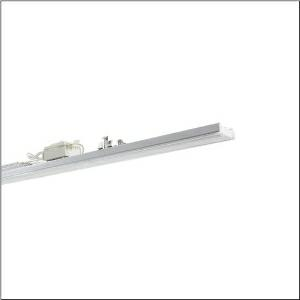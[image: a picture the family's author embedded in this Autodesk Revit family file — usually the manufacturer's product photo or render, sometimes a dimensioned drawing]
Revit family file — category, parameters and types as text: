
# Revit family: licross_r__11_recessed_mo_51tl12dn395g_1cc3
name_source: partatom
category: Lighting Fixtures
units: mm (PartAtom-declared; Revit-internal decimal feet)

## family parameters
Cut with Voids When Loaded = No
Host = Face
Light Source = No
Part Type = Normal
Room Calculation Point = No
Round Connector Dimension = Use Diameter
Shared = No

## types (1)
- --- (1 x LED, 9840 lm, 56.7 W, 3000K)
    Apparent Load = 57 VA
    CIE Flux Codes = 67 92 99 100 100
    Color Rendering = 80
    Color Temperature = 3000K
    Default Elevation = 1800 mm
    Description = Licross® 11 Recessed MO, luminaire insert, of sheet steel, coil coated, white, length: 1.500mm, width: 66mm, height: 67mm, LED rated luminous flux: 9.840lm, light colour: 830, control gear: DALI 2, with plug, 5-pole, with phase selection, mains connection: 220..240V, AC, 50/60Hz, rated input power: 57W, halogen-free wiring, primary optical cover: cover, of PMMA, light emission: direct distribution, primary light characteristic: symmetric, protection rating (complete): IP40, insulation class (complete): insulation class I (protective earthing), certification: CE, ENEC, VDE, UKCA, protection symbol: D if used in an environment without relevant dust loads with corresponding accessories, impact resistance: IK06, permissible ambient temperature for indoor applications: -25..+35°C, corresponds to IFS (International Featured Standards) requirements for safety and quality in the food industry, reducing of maximum allowable ambient temperature of 5°C with ceiling mounting, LABS conformity tested according to VDMA 24364:2018-05, packaging unit: 1 piece
    Height = 58 mm
    Lamp = 1 x LED
    Lamp Light Flux = 9840 lm
    Lamp Power = 56.7 W
    Lamp count = 1
    Length = 1500 mm
    Luminous efficacy = 174 lm/W
    Manufacturer = Siteco
    ModVariant = No
    Model = 51TL12DN395G
    Mounting Place = Ceiling
    Mounting Type = Pendant
    Number of Poles = 1
    OnlyDefault = Yes
    Power Factor = 1
    Product Name = Licross® 11 Recessed MO
    Product group = luminaire insert
    ProductGroupID = 902
    Protection Class = Protection class I
    Protection Degree = IP 40
    RLX_Detail_Level = 1
    RLX_Emergency_Light_Flux = 0 lm
    RLX_Emergency_Type = 0
    RLX_Emergency_Type_DB = No
    RlxData = <blob elided: 24321 chars, md5=6db35950>
    Socket = socket
    Standby Power = 0 W
    System Light Flux = 9840 lm
    System Power = 57 W
    Type Comments = factory setting: luminous flux: 100 % | dim-lin: 254 | 378 mA
    Type Image = l_1296930.jpg
    URL = http://relux.com
    VarID = @adj_068118
    Voltage = 0 V
    Weight = 0.00 kg
    Width = 66 mm

## geometry (parser evidence)
native form markers: Blend x4, Sweep x11
no freeform markers — native parametric forms only
